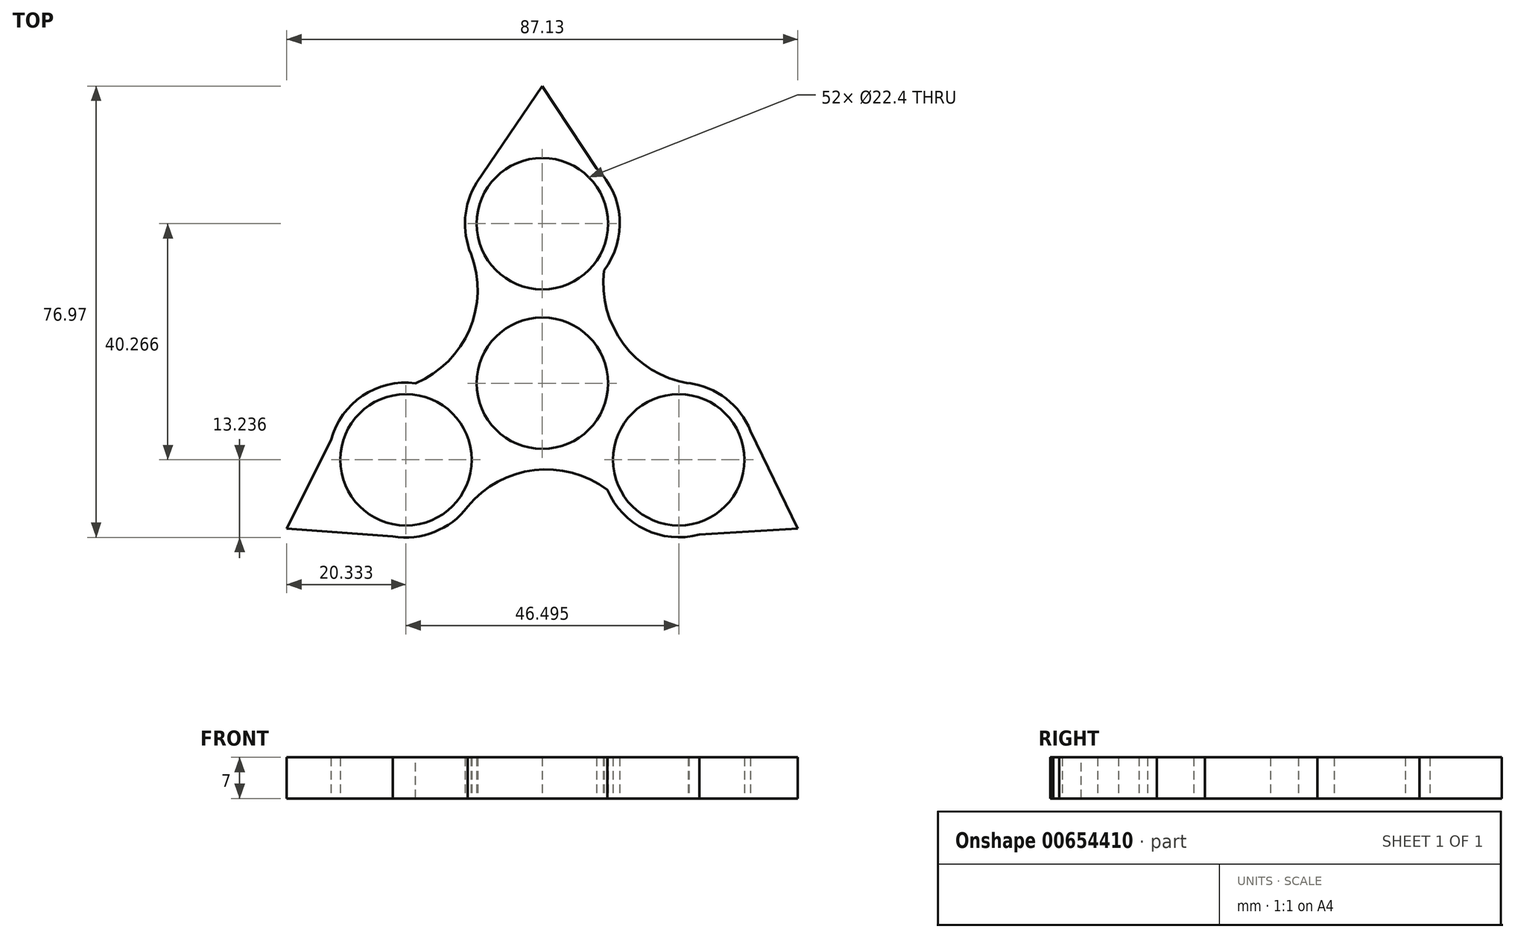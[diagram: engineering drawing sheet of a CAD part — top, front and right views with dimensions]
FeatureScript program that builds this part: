
annotation { "Feature Type Name" : "Feature", "Feature Type Description" : "" }
export const myFeature = defineFeature(function(context is Context, id is Id, definition is map)
    precondition{}
    {
        {
            var Q0;
            Q0=qCreatedBy(makeId("Top.planeOp"),FACE);
            var sketch = newSketch(context, id + "F0", { "sketchPlane" : qUnion([Q0])});
            skCircle(sketch, "E0", {"center": v(0, 0) * mm, "radius": 11.2 * mm});
            skCircle(sketch, "E1", {"center": v(0, 27.2) * mm, "radius": 11.2 * mm});
            skArc(sketch, "E2", {"start": v(10.51, 19.22) * mm, "mid": v(13.17, 28.14) * mm, "end": v(9.27, 36.6) * mm});
            skLineSegment(sketch, "E3.1.0", {"start": v(-12.74, -21.05) * mm, "end": v(-12.74, -21.05) * mm});
            skCircle(sketch, "E3.1.1", {"center": v(-23.25, -13.06) * mm, "radius": 11.2 * mm});
            skArc(sketch, "E3.2.0", {"start": v(11.1, -18.2) * mm, "mid": v(33.75, -21.06) * mm, "end": v(24.97, 0.02) * mm});
            skCircle(sketch, "E3.2.1", {"center": v(23.25, -13.06) * mm, "radius": 11.2 * mm});
            skPoint(sketch, "E3.center", {"position": v(0, 0.36) * mm});
            skArc(sketch, "E4", {"start": v(-21.6, 0) * mm, "mid": v(-12.44, 9.12) * mm, "end": v(-12.16, 22.06) * mm});
            skArc(sketch, "E5.1.0", {"start": v(11.1, -18.2) * mm, "mid": v(-1.4, -14.82) * mm, "end": v(-12.74, -21.05) * mm});
            skArc(sketch, "E5.2.0", {"start": v(10.51, 19.22) * mm, "mid": v(13.82, 6.7) * mm, "end": v(24.89, 0) * mm});
            skPoint(sketch, "E5.center", {"position": v(0, 0.34) * mm});
            skLineSegment(sketch, "E6", {"start": v(-11.2, 34.18) * mm, "end": v(0, 50.67) * mm});
            skLineSegment(sketch, "E7", {"start": v(0, 50.67) * mm, "end": v(9.27, 36.6) * mm});
            skLineSegment(sketch, "E8.1.0", {"start": v(-43.58, -24.78) * mm, "end": v(-36.03, -9.72) * mm});
            skLineSegment(sketch, "E8.1.1", {"start": v(-23.7, -26.24) * mm, "end": v(-43.58, -24.78) * mm});
            skLineSegment(sketch, "E8.2.0", {"start": v(43.55, -24.8) * mm, "end": v(26.76, -25.79) * mm});
            skLineSegment(sketch, "E8.2.1", {"start": v(35.49, -8.13) * mm, "end": v(43.55, -24.8) * mm});
            skPoint(sketch, "E8.center", {"position": v(-0.01, 0.36) * mm});
            skArc(sketch, "E9.1.0", {"start": v(-21.6, 0) * mm, "mid": v(-30.65, -2.15) * mm, "end": v(-36.03, -9.72) * mm});
            skArc(sketch, "E10.trimOffspring", {"start": v(-25.5, -26.1) * mm, "mid": v(-18.4, -25.37) * mm, "end": v(-12.74, -21.05) * mm});
            skArc(sketch, "E11.trimOffspring", {"start": v(-10.61, 35.05) * mm, "mid": v(-13.1, 28.76) * mm, "end": v(-12.16, 22.06) * mm});
            skPoint(sketch, "E12.orphan", {"position": v(26.73, -25.79) * mm});
            skPoint(sketch, "E13.orphan", {"position": v(34.87, -6.85) * mm});
            skLineSegment(sketch, "E14", {"start": v(24.89, 0) * mm, "end": v(24.97, 0.02) * mm});
            skPoint(sketch, "E15.orphan", {"position": v(27.06, -26.33) * mm});
            skPoint(sketch, "E16.orphan", {"position": v(-21.9, -0.5) * mm});
            skSolve(sketch);
        }
        {
            var Q0;
            Q0=makeQuery(id+"F0.imprint","IMPRINT",FACE,{"disambiguationData":[TD([[makeQuery(id+"F0.imprint","IMPRINT",EDGE,{"derivedFrom":sQuery(id+"F0.wireOp",EDGE,"E0")}),-1.0]])]});
            var Q1;
            {var subQ0=sQuery(id+"F0.wireOp",EDGE,"E8.2.0");Q1=makeQuery(id+"F0.imprint","IMPRINT",FACE,{"disambiguationData":[TD([[makeQuery(id+"F0.imprint","IMPRINT",EDGE,{"derivedFrom":subQ0}),-1.0]])]});}
            extrude(context, id + "F1", {"entities" : qUnion([Q0, Q1]), "depth" : 7 * mm, "offsetDistance" : 25 * mm});
        }
    });
